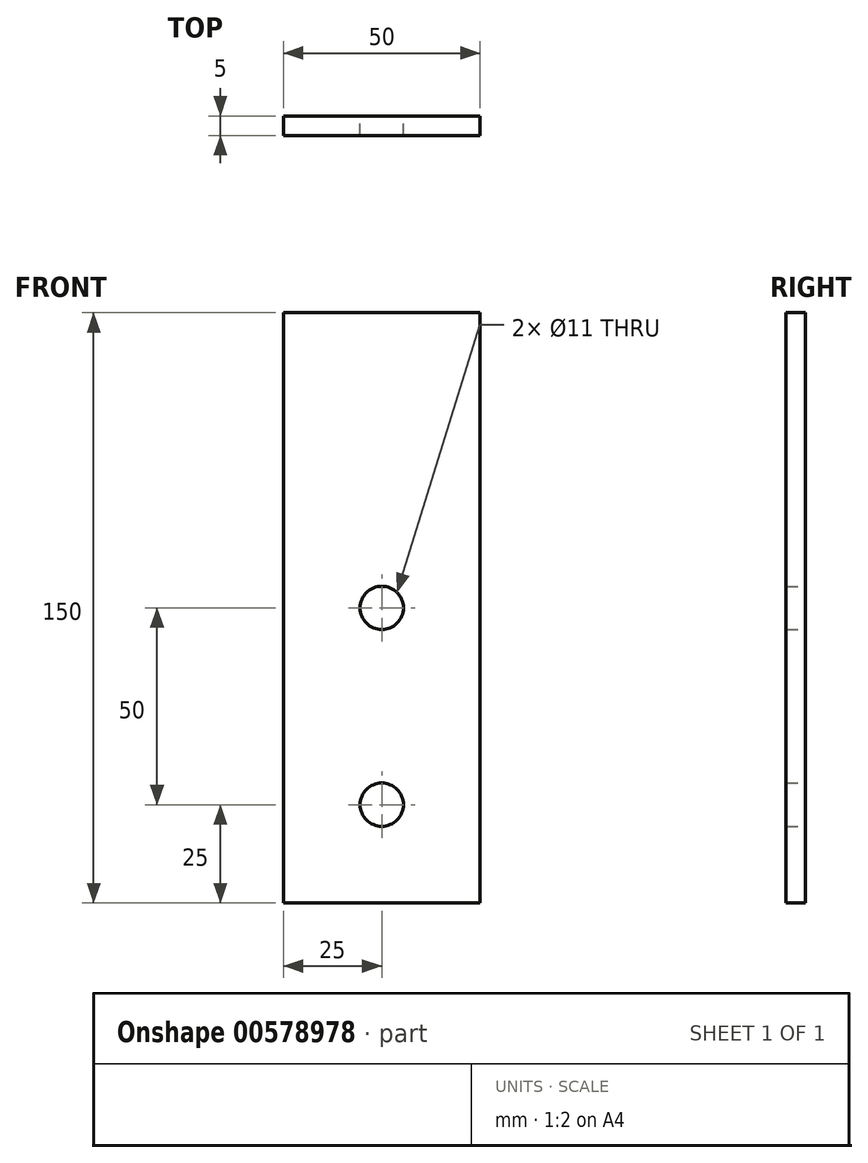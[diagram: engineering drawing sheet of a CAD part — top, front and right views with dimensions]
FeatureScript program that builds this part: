
annotation { "Feature Type Name" : "Feature", "Feature Type Description" : "" }
export const myFeature = defineFeature(function(context is Context, id is Id, definition is map)
    precondition{}
    {
        {
            var Q0;
            Q0=qCreatedBy(makeId("Front.planeOp"),FACE);
            var sketch = newSketch(context, id + "F0", { "sketchPlane" : qUnion([Q0])});
            skLineSegment(sketch, "E0.bottom", {"start": v(25, 75) * mm, "end": v(-25, 75) * mm});
            skLineSegment(sketch, "E0.top", {"start": v(25, -75) * mm, "end": v(-25, -75) * mm});
            skLineSegment(sketch, "E0.left", {"start": v(25, 75) * mm, "end": v(25, -75) * mm});
            skLineSegment(sketch, "E0.right", {"start": v(-25, 75) * mm, "end": v(-25, -75) * mm});
            skPoint(sketch, "E0.middle", {"position": v(0, 0) * mm});
            skCircle(sketch, "E1", {"center": v(0, 0) * mm, "radius": 5.5 * mm});
            skCircle(sketch, "E2", {"center": v(0, -50) * mm, "radius": 5.5 * mm});
            skPoint(sketch, "E2.centerSnap0", {"position": v(0, -75) * mm});
            skSolve(sketch);
        }
        {
            var Q0;
            Q0=makeQuery(id+"F0.imprint","IMPRINT",FACE,{"disambiguationData":[TD([[makeQuery(id+"F0.imprint","IMPRINT",EDGE,{"derivedFrom":sQuery(id+"F0.wireOp",EDGE,"E0.bottom")}),1.0]])]});
            extrude(context, id + "F1", {"entities" : qUnion([Q0]), "endBound" : BoundingType.SYMMETRIC, "depth" : 5 * mm, "offsetDistance" : 25 * mm});
        }
    });
